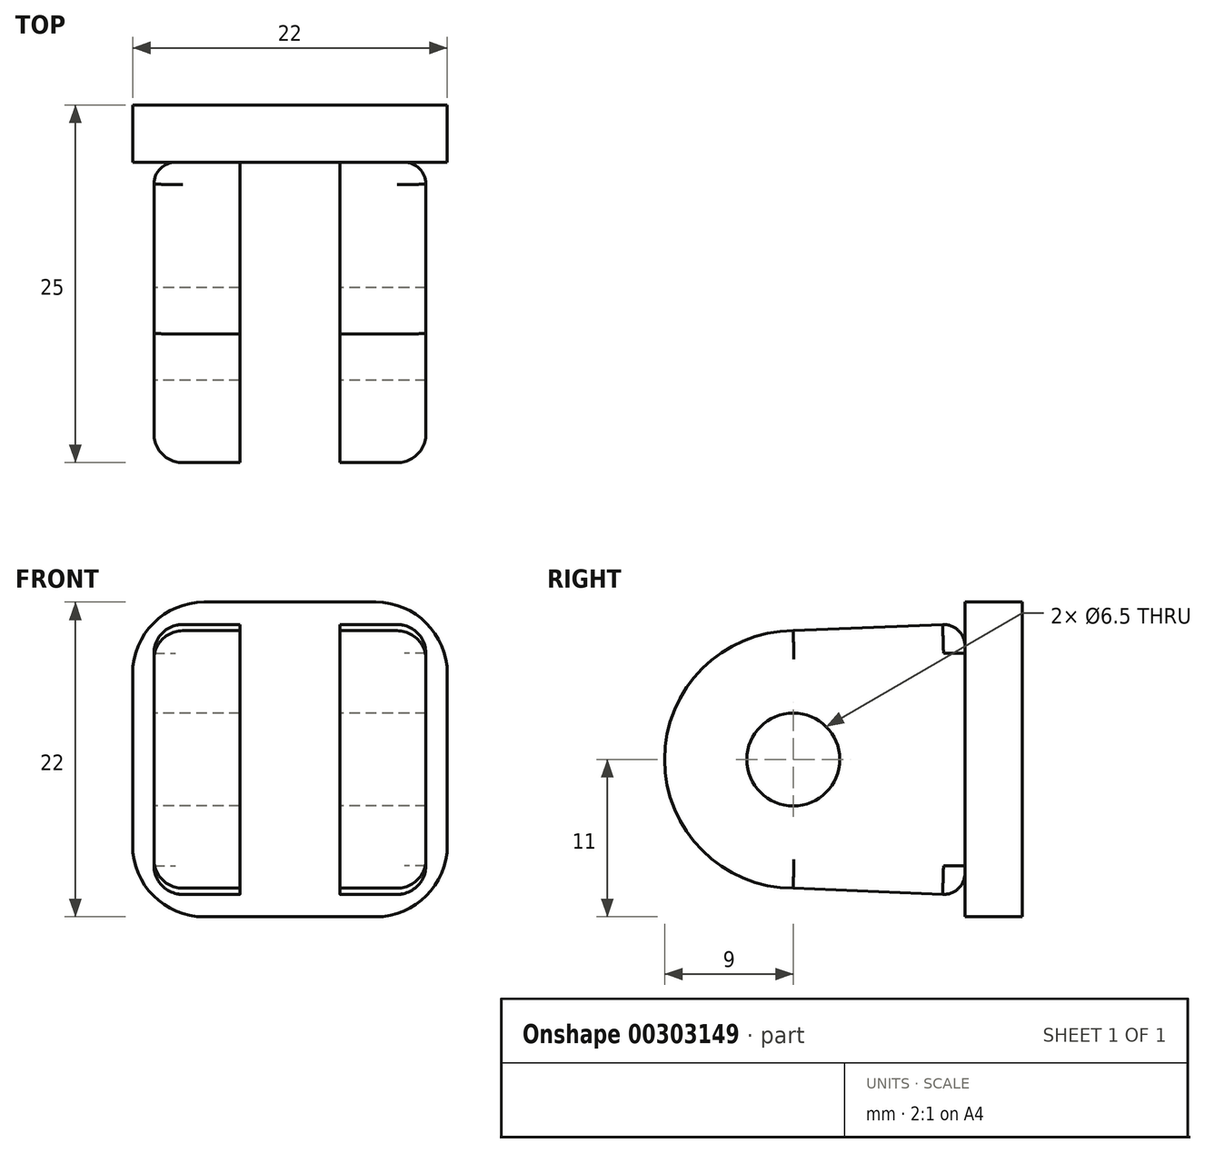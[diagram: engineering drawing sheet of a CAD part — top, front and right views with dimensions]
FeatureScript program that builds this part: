
annotation { "Feature Type Name" : "Feature", "Feature Type Description" : "" }
export const myFeature = defineFeature(function(context is Context, id is Id, definition is map)
    precondition{}
    {
        {
            var Q0;
            Q0=qCreatedBy(makeId("Right.planeOp"),FACE);
            var sketch = newSketch(context, id + "F0", { "sketchPlane" : qUnion([Q0])});
            skArc(sketch, "E0", {"start": v(0, 9) * mm, "mid": v(-9, 0) * mm, "end": v(0, -9) * mm});
            skCircle(sketch, "E1", {"center": v(0, 0) * mm, "radius": 3.25 * mm});
            skLineSegment(sketch, "E2", {"start": v(12, 0) * mm, "end": v(12, 9.5) * mm});
            skLineSegment(sketch, "E3", {"start": v(12, 0) * mm, "end": v(12, -9.5) * mm});
            skLineSegment(sketch, "E4", {"start": v(12, 9.5) * mm, "end": v(0, 9) * mm});
            skLineSegment(sketch, "E5", {"start": v(12, -9.5) * mm, "end": v(0, -9) * mm});
            skSolve(sketch);
        }
        {
            var Q0;
            Q0 = qSketchRegion(id + "F0", true);
            extrude(context, id + "F1", {"entities" : qUnion([Q0]), "depth" : 6 * mm});
        }
        {
            var Q0;
            Q0=makeQuery(id+"F1.opExtrude","SWEPT_BODY",BODY,{"disambiguationData":[OSD([sQuery(id+"F0.wireOp",EDGE,"E0"),sQuery(id+"F0.wireOp",EDGE,"E1"),sQuery(id+"F0.wireOp",EDGE,"E2"),sQuery(id+"F0.wireOp",EDGE,"E3"),sQuery(id+"F0.wireOp",EDGE,"E4"),sQuery(id+"F0.wireOp",EDGE,"E5")])]});
            transform(context, id + "F2", {"entities" : qUnion([Q0]), "transformType" : TransformType.TRANSLATION_3D, "dx" : 3.5 * mm, "dy" : 0 * mm, "dz" : 0 * mm, "makeCopy" : false});
        }
        {
            var Q0;
            Q0=makeQuery(id+"F1.opExtrude","SWEPT_BODY",BODY,{"disambiguationData":[OSD([sQuery(id+"F0.wireOp",EDGE,"E0"),sQuery(id+"F0.wireOp",EDGE,"E1"),sQuery(id+"F0.wireOp",EDGE,"E2"),sQuery(id+"F0.wireOp",EDGE,"E3"),sQuery(id+"F0.wireOp",EDGE,"E4"),sQuery(id+"F0.wireOp",EDGE,"E5")])]});
            transform(context, id + "F3", {"entities" : qUnion([Q0]), "transformType" : TransformType.COPY});
        }
        {
            var Q0;
            Q0=makeQuery(id+"F1.opExtrude","SWEPT_BODY",BODY,{"disambiguationData":[OSD([sQuery(id+"F0.wireOp",EDGE,"E0"),sQuery(id+"F0.wireOp",EDGE,"E1"),sQuery(id+"F0.wireOp",EDGE,"E2"),sQuery(id+"F0.wireOp",EDGE,"E3"),sQuery(id+"F0.wireOp",EDGE,"E4"),sQuery(id+"F0.wireOp",EDGE,"E5")])]});
            transform(context, id + "F4", {"entities" : qUnion([Q0]), "transformType" : TransformType.TRANSLATION_3D, "dx" : -13 * mm, "dy" : 0 * mm, "dz" : 0 * mm, "makeCopy" : false});
        }
        {
            var Q0;
            Q0=qCreatedBy(makeId("Front.planeOp"),FACE);
            var sketch = newSketch(context, id + "F5", { "sketchPlane" : qUnion([Q0])});
            skLineSegment(sketch, "E6.bottom", {"start": v(11, -11) * mm, "end": v(-11, -11) * mm});
            skLineSegment(sketch, "E6.top", {"start": v(11, 11) * mm, "end": v(-11, 11) * mm});
            skLineSegment(sketch, "E6.left", {"start": v(11, -11) * mm, "end": v(11, 11) * mm});
            skLineSegment(sketch, "E6.right", {"start": v(-11, -11) * mm, "end": v(-11, 11) * mm});
            skPoint(sketch, "E6.middle", {"position": v(0, 0) * mm});
            skSolve(sketch);
        }
        {
            var Q0;
            Q0 = qSketchRegion(id + "F5", true);
            extrude(context, id + "F6", {"entities" : qUnion([Q0]), "depth" : 4 * mm});
        }
        {
            var Q0;
            Q0=makeQuery(id+"F6.opExtrude","SWEPT_BODY",BODY,{"disambiguationData":[OSD([sQuery(id+"F5.wireOp",EDGE,"E6.bottom"),sQuery(id+"F5.wireOp",EDGE,"E6.top"),sQuery(id+"F5.wireOp",EDGE,"E6.left"),sQuery(id+"F5.wireOp",EDGE,"E6.right")])]});
            transform(context, id + "F7", {"entities" : qUnion([Q0]), "transformType" : TransformType.TRANSLATION_3D, "dx" : 0 * mm, "dy" : 16 * mm, "dz" : 0 * mm, "makeCopy" : false});
        }
        {
            var Q0;
            Q0=makeQuery(id+"F3.opPattern","COPY",EDGE,{"derivedFrom":makeQuery(id+"F1.opExtrude","CAP_EDGE",EDGE,{"disambiguationData":[OSD([sQuery(id+"F0.wireOp",EDGE,"E0")])],"isStart":false}),"instanceName":"1"});
            var Q1;
            Q1=makeQuery(id+"F1.opExtrude","CAP_EDGE",EDGE,{"disambiguationData":[OSD([sQuery(id+"F0.wireOp",EDGE,"E0")])],"isStart":true});
            fillet(context, id + "F8", {"entities" : qUnion([Q0, Q1]), "radius" : 2 * mm, "tangentPropagation" : true, "allowEdgeOverflow" : false});
        }
        {
            var Q0;
            Q0=makeQuery(id+"F6.opExtrude","SWEPT_EDGE",EDGE,{"disambiguationData":[OSD([sQuery(id+"F5.wireOp",EDGE,"E6.bottom"),sQuery(id+"F5.wireOp",EDGE,"E6.right")])]});
            var Q1;
            Q1=makeQuery(id+"F6.opExtrude","SWEPT_EDGE",EDGE,{"disambiguationData":[OSD([sQuery(id+"F5.wireOp",EDGE,"E6.bottom"),sQuery(id+"F5.wireOp",EDGE,"E6.left")])]});
            var Q2;
            Q2=makeQuery(id+"F6.opExtrude","SWEPT_EDGE",EDGE,{"disambiguationData":[OSD([sQuery(id+"F5.wireOp",EDGE,"E6.top"),sQuery(id+"F5.wireOp",EDGE,"E6.left")])]});
            var Q3;
            Q3=makeQuery(id+"F6.opExtrude","SWEPT_EDGE",EDGE,{"disambiguationData":[OSD([sQuery(id+"F5.wireOp",EDGE,"E6.top"),sQuery(id+"F5.wireOp",EDGE,"E6.right")])]});
            fillet(context, id + "F9", {"entities" : qUnion([Q0, Q1, Q2, Q3]), "radius" : 5 * mm, "tangentPropagation" : true, "allowEdgeOverflow" : false});
        }
        {
            var Q0;
            Q0=makeQuery(id+"F8.opFillet","BLEND_EDGE",EDGE,{"blendedFrom":[makeQuery(id+"F1.opExtrude","CAP_EDGE",EDGE,{"disambiguationData":[OSD([sQuery(id+"F0.wireOp",EDGE,"E5")])],"isStart":true}),makeQuery(id+"F1.opExtrude","SWEPT_FACE",FACE,{"disambiguationData":[OSD([sQuery(id+"F0.wireOp",EDGE,"E2"),sQuery(id+"F0.wireOp",EDGE,"E3")])]})],"blendedInto":[makeQuery(id+"F1.opExtrude","SWEPT_FACE",FACE,{"disambiguationData":[OSD([sQuery(id+"F0.wireOp",EDGE,"E2"),sQuery(id+"F0.wireOp",EDGE,"E3")])]})]});
            var Q1;
            Q1=makeQuery(id+"F3.opPattern","COPY",EDGE,{"derivedFrom":makeQuery(id+"F1.opExtrude","SWEPT_EDGE",EDGE,{"disambiguationData":[OSD([sQuery(id+"F0.wireOp",EDGE,"E3"),sQuery(id+"F0.wireOp",EDGE,"E5")])]}),"instanceName":"1"});
            fillet(context, id + "F10", {"entities" : qUnion([Q0, Q1]), "radius" : 1.5 * mm, "tangentPropagation" : true, "allowEdgeOverflow" : false});
        }
        {
            var Q0;
            Q0=qCreatedBy(makeId("Front.planeOp"),FACE);
            var sketch = newSketch(context, id + "F11", { "sketchPlane" : qUnion([Q0])});
            skLineSegment(sketch, "E7.0", {"start": v(5, 2.89) * mm, "end": v(5, -2.89) * mm});
            skLineSegment(sketch, "E7.1", {"start": v(5, -2.89) * mm, "end": v(0, -5.77) * mm});
            skLineSegment(sketch, "E7.2", {"start": v(0, -5.77) * mm, "end": v(-5, -2.89) * mm});
            skLineSegment(sketch, "E7.3", {"start": v(-5, -2.89) * mm, "end": v(-5, 2.89) * mm});
            skLineSegment(sketch, "E7.4", {"start": v(-5, 2.89) * mm, "end": v(0, 5.77) * mm});
            skLineSegment(sketch, "E7.5", {"start": v(0, 5.77) * mm, "end": v(5, 2.89) * mm});
            skPoint(sketch, "E7.0.midPoint", {"position": v(5, 0) * mm});
            skPoint(sketch, "E8.center.orphan", {"position": v(0, 0) * mm});
            skSolve(sketch);
        }
        {
            var Q0;
            Q0 = qSketchRegion(id + "F11", true);
            extrude(context, id + "F12", {"entities" : qUnion([Q0]), "depth" : 5 * mm});
        }
        {
            var Q0;
            Q0=qCreatedBy(makeId("Front.planeOp"),FACE);
            var sketch = newSketch(context, id + "F13", { "sketchPlane" : qUnion([Q0])});
            skLineSegment(sketch, "E9", {"start": v(0, 0) * mm, "end": v(0, 24.32) * mm, "construction": true});
            skSolve(sketch);
        }
        {
            var Q0;
            Q0=makeQuery(id+"F12.opExtrude","SWEPT_BODY",BODY,{"disambiguationData":[OSD([sQuery(id+"F11.wireOp",EDGE,"E7.0"),sQuery(id+"F11.wireOp",EDGE,"E7.1"),sQuery(id+"F11.wireOp",EDGE,"E7.2"),sQuery(id+"F11.wireOp",EDGE,"E7.3"),sQuery(id+"F11.wireOp",EDGE,"E7.4"),sQuery(id+"F11.wireOp",EDGE,"E7.5")])]});
            var Q1;
            Q1=sQuery(id+"F13.wireOp",EDGE,"E9");
            transform(context, id + "F14", {"entities" : qUnion([Q0]), "transformType" : TransformType.ROTATION, "transformAxis" : qUnion([Q1]), "angle" : 270 * degree, "makeCopy" : false});
        }
        {
            var Q0;
            Q0=makeQuery(id+"F12.opExtrude","SWEPT_BODY",BODY,{"disambiguationData":[OSD([sQuery(id+"F11.wireOp",EDGE,"E7.0"),sQuery(id+"F11.wireOp",EDGE,"E7.1"),sQuery(id+"F11.wireOp",EDGE,"E7.2"),sQuery(id+"F11.wireOp",EDGE,"E7.3"),sQuery(id+"F11.wireOp",EDGE,"E7.4"),sQuery(id+"F11.wireOp",EDGE,"E7.5")])]});
            transform(context, id + "F15", {"entities" : qUnion([Q0]), "transformType" : TransformType.TRANSLATION_3D, "dx" : -6 * mm, "dy" : 0 * mm, "dz" : 0 * mm, "makeCopy" : false});
        }
        {
            var Q0;
            Q0=qCreatedBy(makeId("Front.planeOp"),FACE);
            var sketch = newSketch(context, id + "F16", { "sketchPlane" : qUnion([Q0])});
            skLineSegment(sketch, "E10", {"start": v(0, 0) * mm, "end": v(-32.05, 0) * mm, "construction": true});
            skSolve(sketch);
        }
        {
            var Q0;
            Q0=makeQuery(id+"F12.opExtrude","SWEPT_BODY",BODY,{"disambiguationData":[OSD([sQuery(id+"F11.wireOp",EDGE,"E7.0"),sQuery(id+"F11.wireOp",EDGE,"E7.1"),sQuery(id+"F11.wireOp",EDGE,"E7.2"),sQuery(id+"F11.wireOp",EDGE,"E7.3"),sQuery(id+"F11.wireOp",EDGE,"E7.4"),sQuery(id+"F11.wireOp",EDGE,"E7.5")])]});
            var Q1;
            Q1=sQuery(id+"F16.wireOp",EDGE,"E10");
            transform(context, id + "F17", {"entities" : qUnion([Q0]), "transformType" : TransformType.ROTATION, "transformAxis" : qUnion([Q1]), "angle" : 90 * degree, "makeCopy" : false});
        }
        {
            var Q0;
            Q0=makeQuery(id+"F12.opExtrude","SWEPT_BODY",BODY,{"disambiguationData":[OSD([sQuery(id+"F11.wireOp",EDGE,"E7.0"),sQuery(id+"F11.wireOp",EDGE,"E7.1"),sQuery(id+"F11.wireOp",EDGE,"E7.2"),sQuery(id+"F11.wireOp",EDGE,"E7.3"),sQuery(id+"F11.wireOp",EDGE,"E7.4"),sQuery(id+"F11.wireOp",EDGE,"E7.5")])]});
            var Q1;
            Q1=makeQuery(id+"F6.opExtrude","SWEPT_BODY",BODY,{"disambiguationData":[OSD([sQuery(id+"F5.wireOp",EDGE,"E6.bottom"),sQuery(id+"F5.wireOp",EDGE,"E6.top"),sQuery(id+"F5.wireOp",EDGE,"E6.left"),sQuery(id+"F5.wireOp",EDGE,"E6.right")])]});
            booleanBodies(context, id + "F18", {"operationType" : BooleanOperationType.SUBTRACTION, "tools" : qUnion([Q0]), "targets" : qUnion([Q1])});
        }
    });
